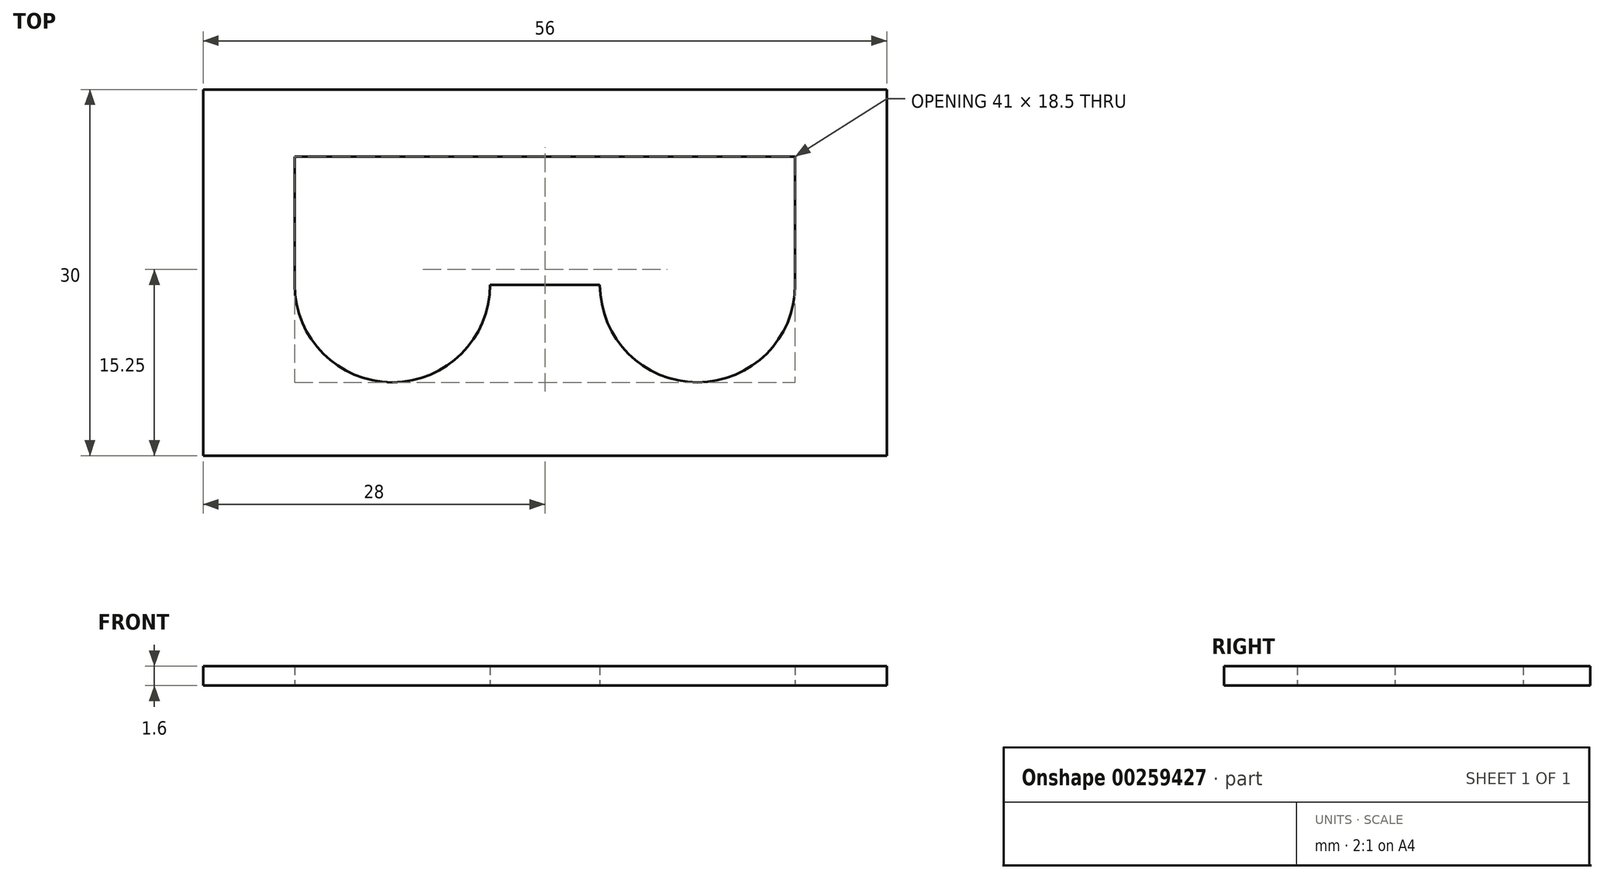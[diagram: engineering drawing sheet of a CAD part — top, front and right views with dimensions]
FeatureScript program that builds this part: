
annotation { "Feature Type Name" : "Feature", "Feature Type Description" : "" }
export const myFeature = defineFeature(function(context is Context, id is Id, definition is map)
    precondition{}
    {
        {
            var Q0;
            Q0=qCreatedBy(makeId("Top.planeOp"),FACE);
            var sketch = newSketch(context, id + "F0", { "sketchPlane" : qUnion([Q0])});
            skLineSegment(sketch, "E0", {"start": v(4.5, -16) * mm, "end": v(-4.5, -16) * mm});
            skArc(sketch, "E1", {"start": v(-20.5, -16) * mm, "mid": v(-12.5, -24) * mm, "end": v(-4.5, -16) * mm});
            skArc(sketch, "E2", {"start": v(4.5, -16) * mm, "mid": v(12.5, -24) * mm, "end": v(20.5, -16) * mm});
            skLineSegment(sketch, "E3", {"start": v(-20.5, -16) * mm, "end": v(-20.5, -5.5) * mm});
            skLineSegment(sketch, "E4", {"start": v(20.5, -16) * mm, "end": v(20.5, -5.5) * mm});
            skLineSegment(sketch, "E5", {"start": v(-20.5, -5.5) * mm, "end": v(20.5, -5.5) * mm});
            skPoint(sketch, "E6.orphan", {"position": v(20.5, 0) * mm});
            skPoint(sketch, "E7.orphan", {"position": v(-20.5, 0) * mm});
            skSolve(sketch);
        }
        {
            var Q0;
            Q0=qSketchRegion(id+"F0",true);
            extrude(context, id + "F1", {"entities" : qUnion([Q0]), "depth" : 1.7 * mm});
        }
        {
            var Q0;
            Q0=qCreatedBy(makeId("Top.planeOp"),FACE);
            var sketch = newSketch(context, id + "F2", { "sketchPlane" : qUnion([Q0])});
            skLineSegment(sketch, "E8", {"start": v(0, 0) * mm, "end": v(-28, 0) * mm});
            skLineSegment(sketch, "E9", {"start": v(-28, 0) * mm, "end": v(-28, -30) * mm});
            skLineSegment(sketch, "E10", {"start": v(-28, -30) * mm, "end": v(28, -30) * mm});
            skLineSegment(sketch, "E11", {"start": v(28, -30) * mm, "end": v(28, 0) * mm});
            skLineSegment(sketch, "E12", {"start": v(28, 0) * mm, "end": v(0, 0) * mm});
            skSolve(sketch);
        }
        {
            var Q0;
            Q0 = qSketchRegion(id + "F2", true);
            extrude(context, id + "F3", {"entities" : qUnion([Q0]), "depth" : 1.6 * mm});
        }
        {
            var Q0;
            Q0=makeQuery(id+"F1.opExtrude","SWEPT_BODY",BODY,{"disambiguationData":[OSD([sQuery(id+"F0.wireOp",EDGE,"E0"),sQuery(id+"F0.wireOp",EDGE,"E1"),sQuery(id+"F0.wireOp",EDGE,"E2"),sQuery(id+"F0.wireOp",EDGE,"E3"),sQuery(id+"F0.wireOp",EDGE,"E4"),sQuery(id+"F0.wireOp",EDGE,"E5")])]});
            var Q1;
            Q1=makeQuery(id+"F3.opExtrude","SWEPT_BODY",BODY,{"disambiguationData":[OSD([sQuery(id+"F2.wireOp",EDGE,"E8"),sQuery(id+"F2.wireOp",EDGE,"E9"),sQuery(id+"F2.wireOp",EDGE,"E10"),sQuery(id+"F2.wireOp",EDGE,"E11"),sQuery(id+"F2.wireOp",EDGE,"E12")])]});
            booleanBodies(context, id + "F4", {"operationType" : BooleanOperationType.SUBTRACTION, "tools" : qUnion([Q0]), "targets" : qUnion([Q1])});
        }
    });
